# Revit family: 306_H7_N
name_source: partatom
category: Pipe Accessories
units: mm (PartAtom-declared; Revit-internal decimal feet)

## family parameters
Always vertical = Yes
Cut with Voids When Loaded = No
Part Type = Valve - Breaks Into
Round Connector Dimension = Use Diameter
Shared = No
Work Plane-Based = No

## types (17) — shared parameters
CAT0 = Yes
Description = Globe valve, 3-way, Flange, PN 16
L2D_Min = 3048 mm
Manufacturer = Belimo
QmdConnectorList = 301;D;302;D;303;D
magiPartTypeId = 306
magiProductFamilyId = H7*N
zero-valued in all types: MC_Default_elevation

## per-type parameters (varying)
| type | BB | BB1 | C | C__ve | D | DB1 | DB2 | DB3 | DB4 | FD | H | HH1 | L2 | L2D | LM | W2D |
| H711N | 26 mm  [stored 0.0853018 ft] | 20 mm  [stored 0.0656168 ft] | 14 mm  [stored 0.0459318 ft] | -14 mm  [stored -0.0459318 ft] | 15 mm | 38 mm  [stored 0.124672 ft] | 76 mm | 34 mm | 61 mm | 95 mm | 65 mm  [stored 0.213255 ft] | 19 mm  [stored 0.062336 ft] | 65 mm  [stored 0.213255 ft] | 130 mm | 102 mm | 15 mm  [stored 0.0492126 ft] |
| H7150N | 196 mm | 147 mm | 26 mm  [stored 0.0853018 ft] | -26 mm  [stored -0.0853018 ft] | 150 mm | 171 mm | 342 mm | 154 mm | 274 mm | 285 mm | 210 mm | 79 mm | 240 mm | 480 mm | 428 mm | 150 mm |
| H7125N | 160 mm | 121 mm | 26 mm  [stored 0.0853018 ft] | -26 mm  [stored -0.0853018 ft] | 125 mm | 150 mm | 300 mm | 135 mm | 240 mm | 250 mm | 200 mm | 74 mm | 200 mm | 400 mm | 348 mm | 125 mm |
| H7100N | 71 mm | 54 mm | 24 mm  [stored 0.0787402 ft] | -24 mm  [stored -0.0787402 ft] | 100 mm | 132 mm | 264 mm | 119 mm | 211 mm | 220 mm | 150 mm | 51 mm  [stored 0.167323 ft] | 175 mm | 350 mm | 302 mm | 100 mm |
| H780N | 63 mm | 47 mm | 22 mm  [stored 0.0721785 ft] | -22 mm  [stored -0.0721785 ft] | 80 mm | 120 mm | 240 mm | 108 mm | 192 mm | 200 mm | 130 mm | 43 mm  [stored 0.141076 ft] | 155 mm | 310 mm | 266 mm | 80 mm |
| H779N | 63 mm | 47 mm | 22 mm  [stored 0.0721785 ft] | -22 mm  [stored -0.0721785 ft] | 80 mm | 120 mm | 240 mm | 108 mm | 192 mm | 200 mm | 130 mm | 43 mm  [stored 0.141076 ft] | 155 mm | 310 mm | 266 mm | 80 mm |
| H765N | 57 mm  [stored 0.187008 ft] | 43 mm  [stored 0.141076 ft] | 20 mm  [stored 0.0656168 ft] | -20 mm  [stored -0.0656168 ft] | 65 mm | 93 mm | 185 mm | 83 mm | 148 mm | 185 mm | 120 mm | 40 mm  [stored 0.131234 ft] | 145 mm | 290 mm | 250 mm | 65 mm  [stored 0.213255 ft] |
| H764N | 57 mm  [stored 0.187008 ft] | 43 mm  [stored 0.141076 ft] | 20 mm  [stored 0.0656168 ft] | -20 mm  [stored -0.0656168 ft] | 65 mm | 93 mm | 185 mm | 83 mm | 148 mm | 185 mm | 120 mm | 40 mm  [stored 0.131234 ft] | 145 mm | 290 mm | 250 mm | 65 mm  [stored 0.213255 ft] |
| H750N | 36 mm | 28 mm | 20 mm  [stored 0.0656168 ft] | -20 mm  [stored -0.0656168 ft] | 50 mm | 66 mm  [stored 0.216535 ft] | 132 mm | 59 mm | 106 mm | 165 mm | 100 mm | 30 mm  [stored 0.0984252 ft] | 115 mm | 230 mm | 190 mm | 50 mm  [stored 0.164042 ft] |
| H740N | 36 mm | 28 mm | 20 mm  [stored 0.0656168 ft] | -20 mm  [stored -0.0656168 ft] | 40 mm | 66 mm  [stored 0.216535 ft] | 132 mm | 59 mm | 106 mm | 165 mm | 100 mm | 30 mm  [stored 0.0984252 ft] | 100 mm | 200 mm | 160 mm | 40 mm  [stored 0.131234 ft] |
| H732N | 32 mm  [stored 0.104987 ft] | 24 mm  [stored 0.0787402 ft] | 18 mm  [stored 0.0590551 ft] | -18 mm  [stored -0.0590551 ft] | 32 mm | 56 mm  [stored 0.183727 ft] | 112 mm | 50 mm  [stored 0.164042 ft] | 90 mm | 140 mm | 95 mm | 30 mm  [stored 0.0984252 ft] | 90 mm | 180 mm | 144 mm | 32 mm  [stored 0.104987 ft] |
| H725N | 30 mm  [stored 0.0984252 ft] | 22 mm  [stored 0.0721785 ft] | 16 mm  [stored 0.0524934 ft] | -16 mm  [stored -0.0524934 ft] | 25 mm | 46 mm  [stored 0.150919 ft] | 92 mm | 41 mm | 74 mm | 115 mm | 75 mm | 22 mm  [stored 0.0721785 ft] | 80 mm | 160 mm | 128 mm | 25 mm  [stored 0.082021 ft] |
| H720N | 26 mm  [stored 0.0853018 ft] | 20 mm  [stored 0.0656168 ft] | 16 mm  [stored 0.0524934 ft] | -16 mm  [stored -0.0524934 ft] | 20 mm | 42 mm  [stored 0.137795 ft] | 84 mm | 38 mm  [stored 0.124672 ft] | 67 mm | 105 mm | 70 mm | 19 mm  [stored 0.062336 ft] | 75 mm | 150 mm | 118 mm | 20 mm  [stored 0.0656168 ft] |
| H715N | 26 mm  [stored 0.0853018 ft] | 20 mm  [stored 0.0656168 ft] | 14 mm  [stored 0.0459318 ft] | -14 mm  [stored -0.0459318 ft] | 15 mm | 38 mm  [stored 0.124672 ft] | 76 mm | 34 mm | 61 mm | 95 mm | 65 mm  [stored 0.213255 ft] | 19 mm  [stored 0.062336 ft] | 65 mm  [stored 0.213255 ft] | 130 mm | 102 mm | 15 mm  [stored 0.0492126 ft] |
| H714N | 26 mm  [stored 0.0853018 ft] | 20 mm  [stored 0.0656168 ft] | 14 mm  [stored 0.0459318 ft] | -14 mm  [stored -0.0459318 ft] | 15 mm | 38 mm  [stored 0.124672 ft] | 76 mm | 34 mm | 61 mm | 95 mm | 65 mm  [stored 0.213255 ft] | 19 mm  [stored 0.062336 ft] | 65 mm  [stored 0.213255 ft] | 130 mm | 102 mm | 15 mm  [stored 0.0492126 ft] |
| H713N | 26 mm  [stored 0.0853018 ft] | 20 mm  [stored 0.0656168 ft] | 14 mm  [stored 0.0459318 ft] | -14 mm  [stored -0.0459318 ft] | 15 mm | 38 mm  [stored 0.124672 ft] | 76 mm | 34 mm | 61 mm | 95 mm | 65 mm  [stored 0.213255 ft] | 19 mm  [stored 0.062336 ft] | 65 mm  [stored 0.213255 ft] | 130 mm | 102 mm | 15 mm  [stored 0.0492126 ft] |
| H712N | 26 mm  [stored 0.0853018 ft] | 20 mm  [stored 0.0656168 ft] | 14 mm  [stored 0.0459318 ft] | -14 mm  [stored -0.0459318 ft] | 15 mm | 38 mm  [stored 0.124672 ft] | 76 mm | 34 mm | 61 mm | 95 mm | 65 mm  [stored 0.213255 ft] | 19 mm  [stored 0.062336 ft] | 65 mm  [stored 0.213255 ft] | 130 mm | 102 mm | 15 mm  [stored 0.0492126 ft] |

note: column(s) folded — value = type name in every type: magiProductCode, magiProductId

note: [stored X ft] marks values corroborated as IEEE doubles in the binary element streams (Revit-internal decimal feet)

## geometry (parser evidence)
native form markers: Sweep x2
no freeform markers — native parametric forms only
